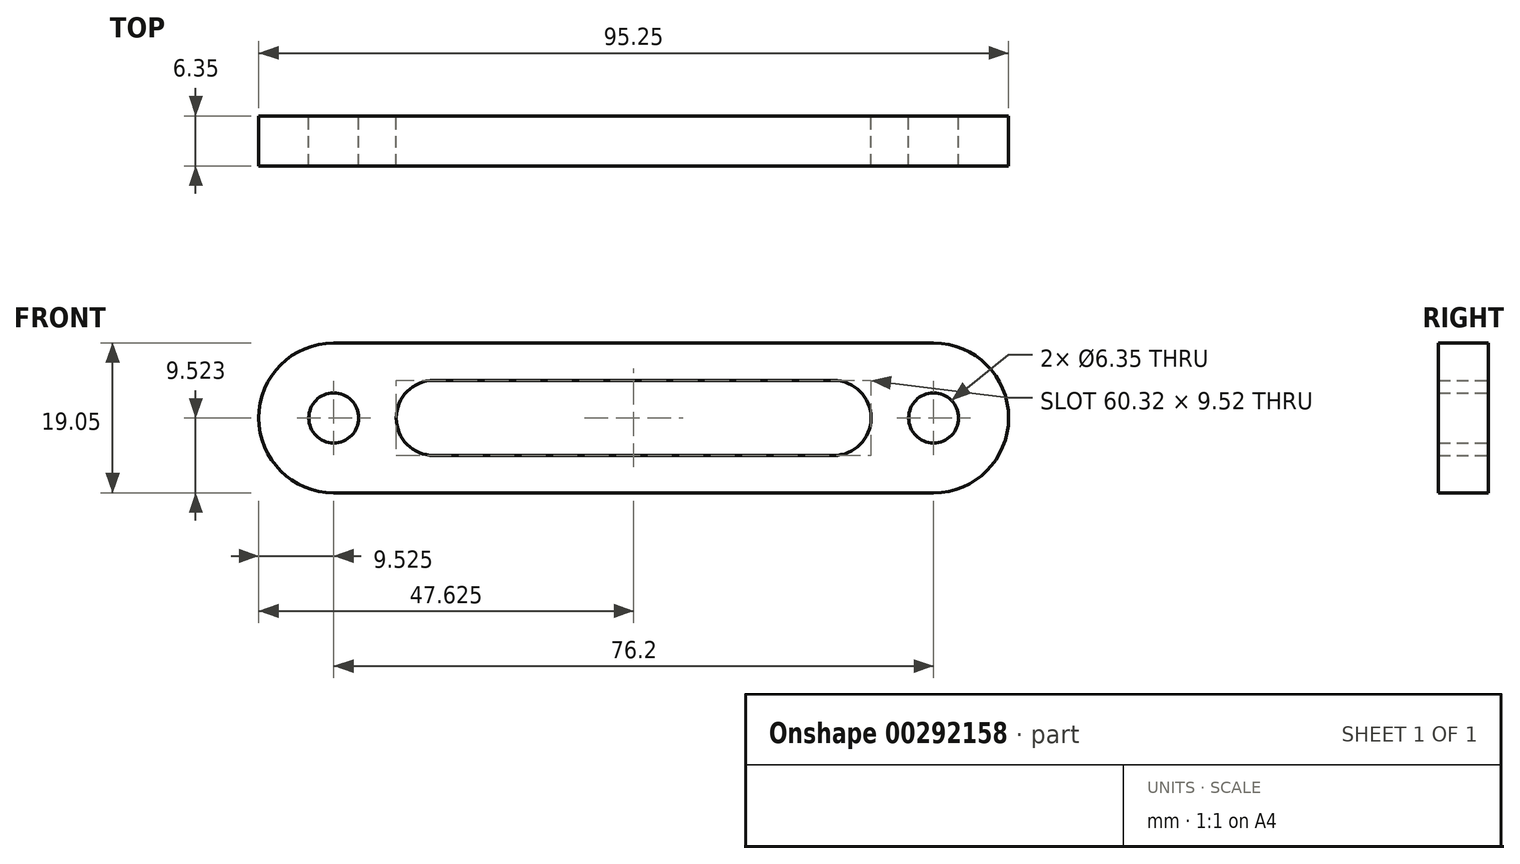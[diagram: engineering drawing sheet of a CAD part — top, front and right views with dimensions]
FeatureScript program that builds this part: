
annotation { "Feature Type Name" : "Feature", "Feature Type Description" : "" }
export const myFeature = defineFeature(function(context is Context, id is Id, definition is map)
    precondition{}
    {
        {
            var Q0;
            Q0=qCreatedBy(makeId("Front.planeOp"),FACE);
            var sketch = newSketch(context, id + "F0", { "sketchPlane" : qUnion([Q0])});
            skLineSegment(sketch, "E0.bottom", {"start": v(-9.53, -11.2) * mm, "end": v(66.67, -11.2) * mm});
            skLineSegment(sketch, "E0.top", {"start": v(-9.53, -30.25) * mm, "end": v(66.67, -30.25) * mm});
            skArc(sketch, "E1", {"start": v(-9.53, -11.2) * mm, "mid": v(-19.05, -20.73) * mm, "end": v(-9.53, -30.25) * mm});
            skArc(sketch, "E2", {"start": v(66.67, -30.25) * mm, "mid": v(76.2, -20.73) * mm, "end": v(66.67, -11.2) * mm});
            skCircle(sketch, "E3", {"center": v(-9.53, -20.73) * mm, "radius": 3.18 * mm});
            skCircle(sketch, "E4", {"center": v(66.67, -20.73) * mm, "radius": 3.18 * mm});
            skLineSegment(sketch, "E5", {"start": v(3.17, -20.73) * mm, "end": v(3.17, -15.97) * mm});
            skLineSegment(sketch, "E6", {"start": v(3.17, -25.5) * mm, "end": v(53.97, -25.5) * mm});
            skLineSegment(sketch, "E7", {"start": v(3.17, -15.97) * mm, "end": v(53.97, -15.97) * mm});
            skArc(sketch, "E8", {"start": v(3.17, -15.97) * mm, "mid": v(-1.59, -20.73) * mm, "end": v(3.17, -25.5) * mm});
            skArc(sketch, "E9", {"start": v(53.97, -25.5) * mm, "mid": v(58.74, -20.73) * mm, "end": v(53.97, -15.97) * mm});
            skSolve(sketch);
        }
        {
            var Q0;
            Q0 = qSketchRegion(id + "F0", true);
            extrude(context, id + "F1", {"entities" : qUnion([Q0]), "depth" : 6.35 * mm});
        }
    });
